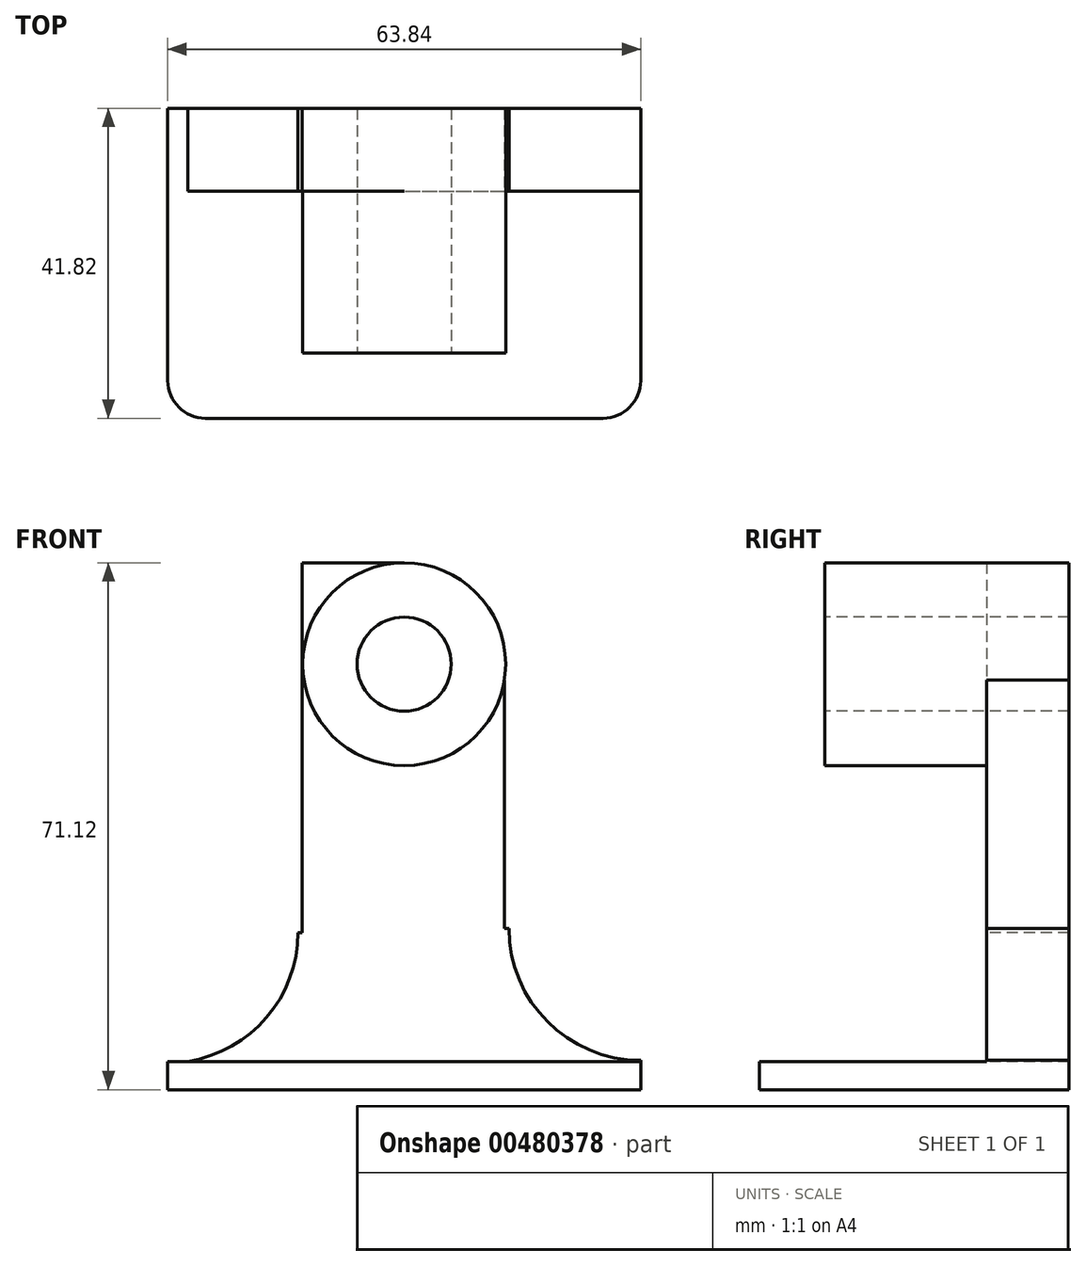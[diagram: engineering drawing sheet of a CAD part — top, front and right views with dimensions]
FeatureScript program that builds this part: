
annotation { "Feature Type Name" : "Feature", "Feature Type Description" : "" }
export const myFeature = defineFeature(function(context is Context, id is Id, definition is map)
    precondition{}
    {
        {
            var Q0;
            Q0=qCreatedBy(makeId("Top.planeOp"),FACE);
            var sketch = newSketch(context, id + "F0", { "sketchPlane" : qUnion([Q0])});
            skLineSegment(sketch, "E0.bottom", {"start": v(-31.92, 20.9) * mm, "end": v(31.92, 20.9) * mm});
            skLineSegment(sketch, "E0.top", {"start": v(-31.92, -20.9) * mm, "end": v(31.92, -20.9) * mm});
            skLineSegment(sketch, "E0.left", {"start": v(-31.92, 20.9) * mm, "end": v(-31.92, -20.9) * mm});
            skLineSegment(sketch, "E0.right", {"start": v(31.92, 20.9) * mm, "end": v(31.92, -20.9) * mm});
            skPoint(sketch, "E0.middle", {"position": v(0, 0) * mm});
            skSolve(sketch);
        }
        {
            var Q0;
            Q0=makeQuery(id+"F0.imprint","IMPRINT",FACE,{"disambiguationData":[TD([[makeQuery(id+"F0.imprint","IMPRINT",EDGE,{"derivedFrom":sQuery(id+"F0.wireOp",EDGE,"E0.bottom")}),-1.0]])]});
            extrude(context, id + "F1", {"entities" : qUnion([Q0]), "depth" : 3.8 * mm});
        }
        {
            var Q0;
            Q0=makeQuery(id+"F1.opExtrude","SWEPT_EDGE",EDGE,{"disambiguationData":[OSD([sQuery(id+"F0.wireOp",EDGE,"E0.top"),sQuery(id+"F0.wireOp",EDGE,"E0.left")])]});
            var Q1;
            Q1=makeQuery(id+"F1.opExtrude","SWEPT_EDGE",EDGE,{"disambiguationData":[OSD([sQuery(id+"F0.wireOp",EDGE,"E0.top"),sQuery(id+"F0.wireOp",EDGE,"E0.right")])]});
            fillet(context, id + "F2", {"entities" : qUnion([Q0, Q1]), "radius" : 5.08 * mm, "tangentPropagation" : true, "allowEdgeOverflow" : false});
        }
        {
            var Q0;
            Q0=makeQuery(id+"F1.opExtrude","CAP_FACE",FACE,{"disambiguationData":[OSD([sQuery(id+"F0.wireOp",EDGE,"E0.bottom"),sQuery(id+"F0.wireOp",EDGE,"E0.top"),sQuery(id+"F0.wireOp",EDGE,"E0.left"),sQuery(id+"F0.wireOp",EDGE,"E0.right")])],"isStart":false});
            var sketch = newSketch(context, id + "F3", { "sketchPlane" : qUnion([Q0])});
            skLineSegment(sketch, "E1.bottom", {"start": v(-31.92, 20.9) * mm, "end": v(31.92, 20.9) * mm});
            skLineSegment(sketch, "E1.top", {"start": v(-31.92, 9.76) * mm, "end": v(31.92, 9.76) * mm});
            skLineSegment(sketch, "E1.left", {"start": v(-31.92, 20.9) * mm, "end": v(-31.92, 9.76) * mm});
            skLineSegment(sketch, "E1.right", {"start": v(31.92, 20.9) * mm, "end": v(31.92, 9.76) * mm});
            skSolve(sketch);
        }
        {
            var Q0;
            Q0=makeQuery(id+"F3.imprint","IMPRINT",FACE,{"disambiguationData":[TD([[makeQuery(id+"F3.imprint","IMPRINT",EDGE,{"derivedFrom":sQuery(id+"F3.wireOp",EDGE,"E1.bottom")}),-1.0]])]});
            extrude(context, id + "F4", {"entities" : qUnion([Q0]), "operationType" : NewBodyOperationType.ADD, "depth" : 67.3 * mm});
        }
        {
            var Q0;
            Q0=makeQuery(id+"F4.opExtrude","SWEPT_FACE",FACE,{"disambiguationData":[OSD([sQuery(id+"F3.wireOp",EDGE,"E1.top")])]});
            var sketch = newSketch(context, id + "F5", { "sketchPlane" : qUnion([Q0])});
            skCircle(sketch, "E2", {"center": v(0, 57.43) * mm, "radius": 13.7 * mm});
            skSolve(sketch);
        }
        {
            var Q0;
            Q0=makeQuery(id+"F5.imprint","IMPRINT",FACE,{"disambiguationData":[TD([[makeQuery(id+"F5.imprint","IMPRINT",EDGE,{"derivedFrom":sQuery(id+"F5.wireOp",EDGE,"E2")}),1.0]])]});
            extrude(context, id + "F6", {"entities" : qUnion([Q0]), "operationType" : NewBodyOperationType.ADD, "depth" : 21.84 * mm});
        }
        {
            var Q0;
            Q0=makeQuery(id+"F6.opExtrude","CAP_FACE",FACE,{"disambiguationData":[OSD([sQuery(id+"F5.wireOp",EDGE,"E2")])],"isStart":false});
            var sketch = newSketch(context, id + "F7", { "sketchPlane" : qUnion([Q0])});
            skPoint(sketch, "E3", {"position": v(0, 57.43) * mm});
            skSolve(sketch);
        }
        {
            var Q0;
            Q0=sQuery(id+"F7.wireOp",VERTEX,"E3");
            var Q1;
            Q1=makeQuery(id+"F1.opExtrude","SWEPT_BODY",BODY,{"disambiguationData":[OSD([sQuery(id+"F0.wireOp",EDGE,"E0.bottom"),sQuery(id+"F0.wireOp",EDGE,"E0.top"),sQuery(id+"F0.wireOp",EDGE,"E0.left"),sQuery(id+"F0.wireOp",EDGE,"E0.right")])]});
            hole(context, id + "F8", {"style" : HoleStyle.SIMPLE, "endStyle" : HoleEndStyle.THROUGH, "holeDiameter" : 12.7 * mm, "isTappedThrough" : true, "tappedDepth" : 12.7 * mm, "tapClearance" : 3, "locations" : qUnion([Q0]), "scope" : qUnion([Q1])});
        }
        {
            var Q0;
            Q0=makeQuery(id+"F4.opExtrude","SWEPT_FACE",FACE,{"disambiguationData":[OSD([sQuery(id+"F3.wireOp",EDGE,"E1.top")])]});
            var sketch = newSketch(context, id + "F9", { "sketchPlane" : qUnion([Q0])});
            skLineSegment(sketch, "E4.bottom", {"start": v(-31.92, 71.12) * mm, "end": v(-13.8, 71.12) * mm});
            skLineSegment(sketch, "E4.top", {"start": v(-31.92, 21.19) * mm, "end": v(-13.8, 21.19) * mm});
            skLineSegment(sketch, "E4.right", {"start": v(-13.8, 71.12) * mm, "end": v(-13.8, 21.19) * mm});
            skLineSegment(sketch, "E5.bottom", {"start": v(31.92, 71.12) * mm, "end": v(13.52, 71.12) * mm});
            skLineSegment(sketch, "E5.top", {"start": v(31.92, 21.74) * mm, "end": v(13.52, 21.74) * mm});
            skLineSegment(sketch, "E5.left", {"start": v(31.92, 71.12) * mm, "end": v(31.92, 21.74) * mm});
            skLineSegment(sketch, "E5.right", {"start": v(13.52, 71.12) * mm, "end": v(13.52, 21.74) * mm});
            skSolve(sketch);
        }
        {
            var Q0;
            {var subQ0=sQuery(id+"F9.wireOp",EDGE,"E4.bottom");Q0=makeQuery(id+"F9.imprint","IMPRINT",FACE,{"disambiguationData":[TD([[makeQuery(id+"F9.imprint","IMPRINT",EDGE,{"derivedFrom":subQ0}),-1.0]])]});}
            var Q1;
            {var subQ1=sQuery(id+"F9.wireOp",EDGE,"E5.bottom");Q1=makeQuery(id+"F9.imprint","IMPRINT",FACE,{"disambiguationData":[TD([[makeQuery(id+"F9.imprint","IMPRINT",EDGE,{"derivedFrom":subQ1}),-1.0]])]});}
            extrude(context, id + "F10", {"entities" : qUnion([Q0, Q1]), "operationType" : NewBodyOperationType.REMOVE, "oppositeDirection" : true, "depth" : 25.4 * mm});
        }
        {
            var Q0;
            {var subQ4=sQuery(id+"F3.wireOp",EDGE,"E1.top");var subQ5=makeQuery(id+"F4.opExtrude","SWEPT_FACE",FACE,{"disambiguationData":[OSD([subQ4])]});var subQ7=sQuery(id+"F0.wireOp",EDGE,"E0.left");Q0=makeQuery(id+"F10.boolean.opBoolean","SPLIT",FACE,{"disambiguationData":[TD([makeQuery(id+"F1.opExtrude","SWEPT_FACE",FACE,{"disambiguationData":[OSD([subQ7])]})])],"derivedFrom":subQ5});}
            var sketch = newSketch(context, id + "F11", { "sketchPlane" : qUnion([Q0])});
            skCircle(sketch, "E6", {"center": v(-31.92, 21.19) * mm, "radius": 17.58 * mm});
            skCircle(sketch, "E7", {"center": v(31.92, 21.74) * mm, "radius": 17.78 * mm});
            skSolve(sketch);
        }
        {
            var Q0;
            {var subQ1=sQuery(id+"F3.wireOp",EDGE,"E1.top");var subQ6=makeQuery(id+"F4.opExtrude","SWEPT_EDGE",EDGE,{"disambiguationData":[OSD([sQuery(id+"F0.wireOp",EDGE,"E0.left"),subQ1,sQuery(id+"F3.wireOp",EDGE,"E1.left")])]});Q0=makeQuery(id+"F11.imprint","IMPRINT",FACE,{"disambiguationData":[TD([[makeQuery(id+"F11.imprint","IMPRINT",EDGE,{"derivedFrom":subQ6}),1.0]])]});}
            var Q1;
            {var subQ0=sQuery(id+"F11.wireOp",EDGE,"E7");var subQ1=makeQuery(id+"F10.boolean.opBoolean","COPY",EDGE,{"derivedFrom":makeQuery(id+"F10.opExtrude","CAP_EDGE",EDGE,{"disambiguationData":[OSD([sQuery(id+"F9.wireOp",EDGE,"E5.top")])],"isStart":true})});var subQ2=makeQuery(id+"F11.imprint","INTERSECT",VERTEX,{"derivedFrom":[subQ1,subQ0]});Q1=makeQuery(id+"F11.imprint","IMPRINT",FACE,{"disambiguationData":[TD([[makeQuery(id+"F11.imprint","IMPRINT",EDGE,{"disambiguationData":[TD([[subQ2,-1.0]])],"derivedFrom":subQ0}),1.0]])]});}
            extrude(context, id + "F12", {"entities" : qUnion([Q0, Q1]), "operationType" : NewBodyOperationType.REMOVE, "oppositeDirection" : true, "depth" : 25.4 * mm});
        }
        {
            var Q0;
            {var subQ0=sQuery(id+"F9.wireOp",EDGE,"E5.right");var subQ2=sQuery(id+"F5.wireOp",EDGE,"E2");var subQ4=sQuery(id+"F3.wireOp",EDGE,"E1.top");var subQ5=makeQuery(id+"F4.opExtrude","SWEPT_FACE",FACE,{"disambiguationData":[OSD([subQ4])]});Q0=makeQuery(id+"F10.boolean.opBoolean","SPLIT",FACE,{"disambiguationData":[TD([makeQuery(id+"F10.opExtrude","SWEPT_FACE",FACE,{"disambiguationData":[OSD([subQ0]),TDD([makeQuery(id+"F9.imprint","IMPRINT",EDGE,{"disambiguationData":[TD([[makeQuery(id+"F9.imprint","INTERSECT",VERTEX,{"disambiguationData":[OD(0.0)],"derivedFrom":[makeQuery(id+"F6.opExtrude","CAP_EDGE",EDGE,{"disambiguationData":[OSD([subQ2])],"isStart":true}),subQ0]}),1.0]])],"derivedFrom":subQ0})])]})])],"derivedFrom":subQ5});}
            extrude(context, id + "F13", {"entities" : qUnion([Q0]), "operationType" : NewBodyOperationType.REMOVE, "oppositeDirection" : true, "depth" : 25.4 * mm});
        }
    });
